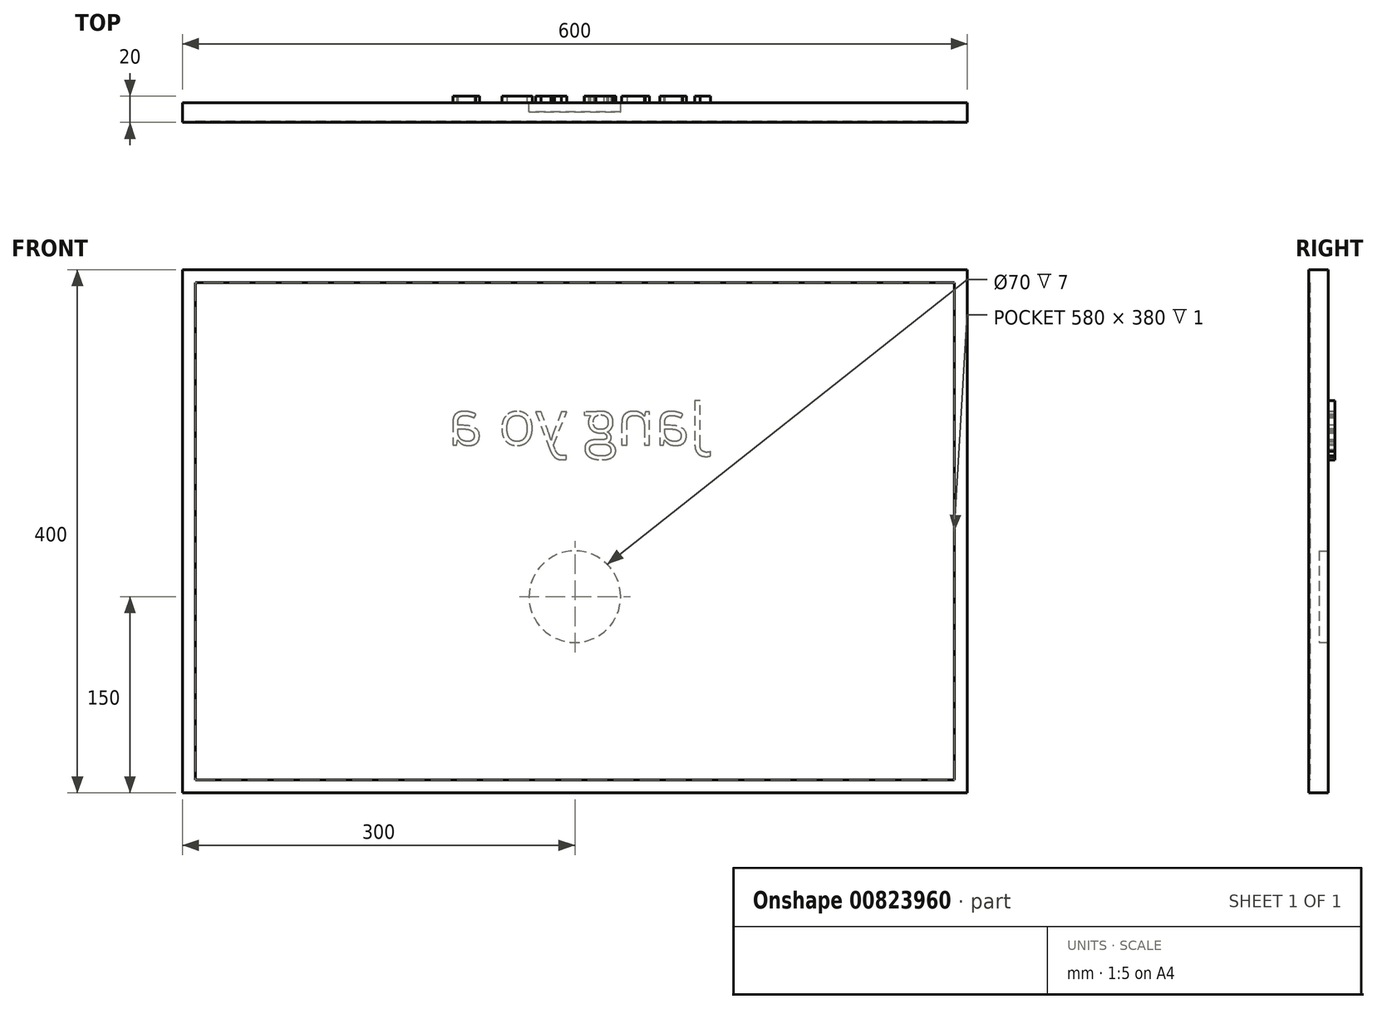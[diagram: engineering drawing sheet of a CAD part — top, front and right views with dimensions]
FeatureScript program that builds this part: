
annotation { "Feature Type Name" : "Feature", "Feature Type Description" : "" }
export const myFeature = defineFeature(function(context is Context, id is Id, definition is map)
    precondition{}
    {
        {
            var Q0;
            Q0=qCreatedBy(makeId("Front.planeOp"),FACE);
            var sketch = newSketch(context, id + "F0", { "sketchPlane" : qUnion([Q0])});
            skLineSegment(sketch, "E0.bottom", {"start": v(-300, 400) * mm, "end": v(300, 400) * mm});
            skLineSegment(sketch, "E0.top", {"start": v(-300, 0) * mm, "end": v(300, 0) * mm});
            skLineSegment(sketch, "E0.left", {"start": v(-300, 400) * mm, "end": v(-300, 0) * mm});
            skLineSegment(sketch, "E0.right", {"start": v(300, 400) * mm, "end": v(300, 0) * mm});
            skLineSegment(sketch, "E1.0", {"start": v(-290, 390) * mm, "end": v(290, 390) * mm});
            skLineSegment(sketch, "E1.1", {"start": v(-290, 390) * mm, "end": v(-290, 10) * mm});
            skLineSegment(sketch, "E1.2", {"start": v(-290, 10) * mm, "end": v(290, 10) * mm});
            skLineSegment(sketch, "E1.3", {"start": v(290, 390) * mm, "end": v(290, 10) * mm});
            skSolve(sketch);
        }
        {
            var Q0;
            Q0=makeQuery(id+"F0.imprint","IMPRINT",FACE,{"disambiguationData":[TD([[makeQuery(id+"F0.imprint","IMPRINT",EDGE,{"derivedFrom":sQuery(id+"F0.wireOp",EDGE,"E0.bottom")}),-1.0]])]});
            var Q1;
            Q1=makeQuery(id+"F0.imprint","IMPRINT",FACE,{"disambiguationData":[TD([[makeQuery(id+"F0.imprint","IMPRINT",EDGE,{"derivedFrom":sQuery(id+"F0.wireOp",EDGE,"E1.0")}),-1.0]])]});
            extrude(context, id + "F1", {"entities" : qUnion([Q0, Q1]), "depth" : 15 * mm, "offsetDistance" : 25 * mm});
        }
        {
            var Q0;
            Q0=makeQuery(id+"F1.opExtrude","CAP_FACE",FACE,{"disambiguationData":[OSD([sQuery(id+"F0.wireOp",EDGE,"E0.bottom"),sQuery(id+"F0.wireOp",EDGE,"E0.top"),sQuery(id+"F0.wireOp",EDGE,"E0.left"),sQuery(id+"F0.wireOp",EDGE,"E0.right")])],"isStart":false});
            var sketch = newSketch(context, id + "F2", { "sketchPlane" : qUnion([Q0])});
            skLineSegment(sketch, "E2.0", {"start": v(-290, 390) * mm, "end": v(290, 390) * mm});
            skLineSegment(sketch, "E2.1", {"start": v(-290, 390) * mm, "end": v(-290, 10) * mm});
            skLineSegment(sketch, "E2.2", {"start": v(-290, 10) * mm, "end": v(290, 10) * mm});
            skLineSegment(sketch, "E2.3", {"start": v(290, 390) * mm, "end": v(290, 10) * mm});
            skSolve(sketch);
        }
        {
            var Q0;
            Q0=makeQuery(id+"F2.imprint","IMPRINT",FACE,{"disambiguationData":[TD([[makeQuery(id+"F2.imprint","IMPRINT",EDGE,{"derivedFrom":sQuery(id+"F2.wireOp",EDGE,"E2.0")}),-1.0]])]});
            extrude(context, id + "F3", {"entities" : qUnion([Q0]), "operationType" : NewBodyOperationType.REMOVE, "oppositeDirection" : true, "depth" : 1 * mm, "offsetDistance" : 25 * mm});
        }
        {
            var Q0;
            Q0=makeQuery(id+"F1.opExtrude","CAP_FACE",FACE,{"disambiguationData":[OSD([sQuery(id+"F0.wireOp",EDGE,"E0.bottom"),sQuery(id+"F0.wireOp",EDGE,"E0.top"),sQuery(id+"F0.wireOp",EDGE,"E0.left"),sQuery(id+"F0.wireOp",EDGE,"E0.right")])],"isStart":true});
            var sketch = newSketch(context, id + "F4", { "sketchPlane" : qUnion([Q0])});
            skCircle(sketch, "E3", {"center": v(0, 150) * mm, "radius": 35 * mm});
            skSolve(sketch);
        }
        {
            var Q0;
            Q0=makeQuery(id+"F4.imprint","IMPRINT",FACE,{"disambiguationData":[TD([[makeQuery(id+"F4.imprint","IMPRINT",EDGE,{"derivedFrom":sQuery(id+"F4.wireOp",EDGE,"E3")}),1.0]])]});
            extrude(context, id + "F5", {"entities" : qUnion([Q0]), "operationType" : NewBodyOperationType.REMOVE, "oppositeDirection" : true, "depth" : 7 * mm, "offsetDistance" : 25 * mm});
        }
        {
            var Q0;
            Q0=makeQuery(id+"F1.opExtrude","CAP_FACE",FACE,{"disambiguationData":[OSD([sQuery(id+"F0.wireOp",EDGE,"E0.bottom"),sQuery(id+"F0.wireOp",EDGE,"E0.top"),sQuery(id+"F0.wireOp",EDGE,"E0.left"),sQuery(id+"F0.wireOp",EDGE,"E0.right")])],"isStart":true});
            var sketch = newSketch(context, id + "F6", { "sketchPlane" : qUnion([Q0])});
            skText(sketch, "E4", { "text": "Jang yo a", "fontName": "OpenSans-Regular.ttf"});
            const initialGuessF6  = {"E4": [-0.1, 0.26596, 1, 0, 0.03404]};
            skSetInitialGuess(sketch, initialGuessF6);
            skSolve(sketch);
        }
        {
            var Q0;
            Q0 = qSketchRegion(id + "F6", true);
            extrude(context, id + "F7", {"entities" : qUnion([Q0]), "operationType" : NewBodyOperationType.ADD, "depth" : 5 * mm, "offsetDistance" : 25 * mm});
        }
    });
